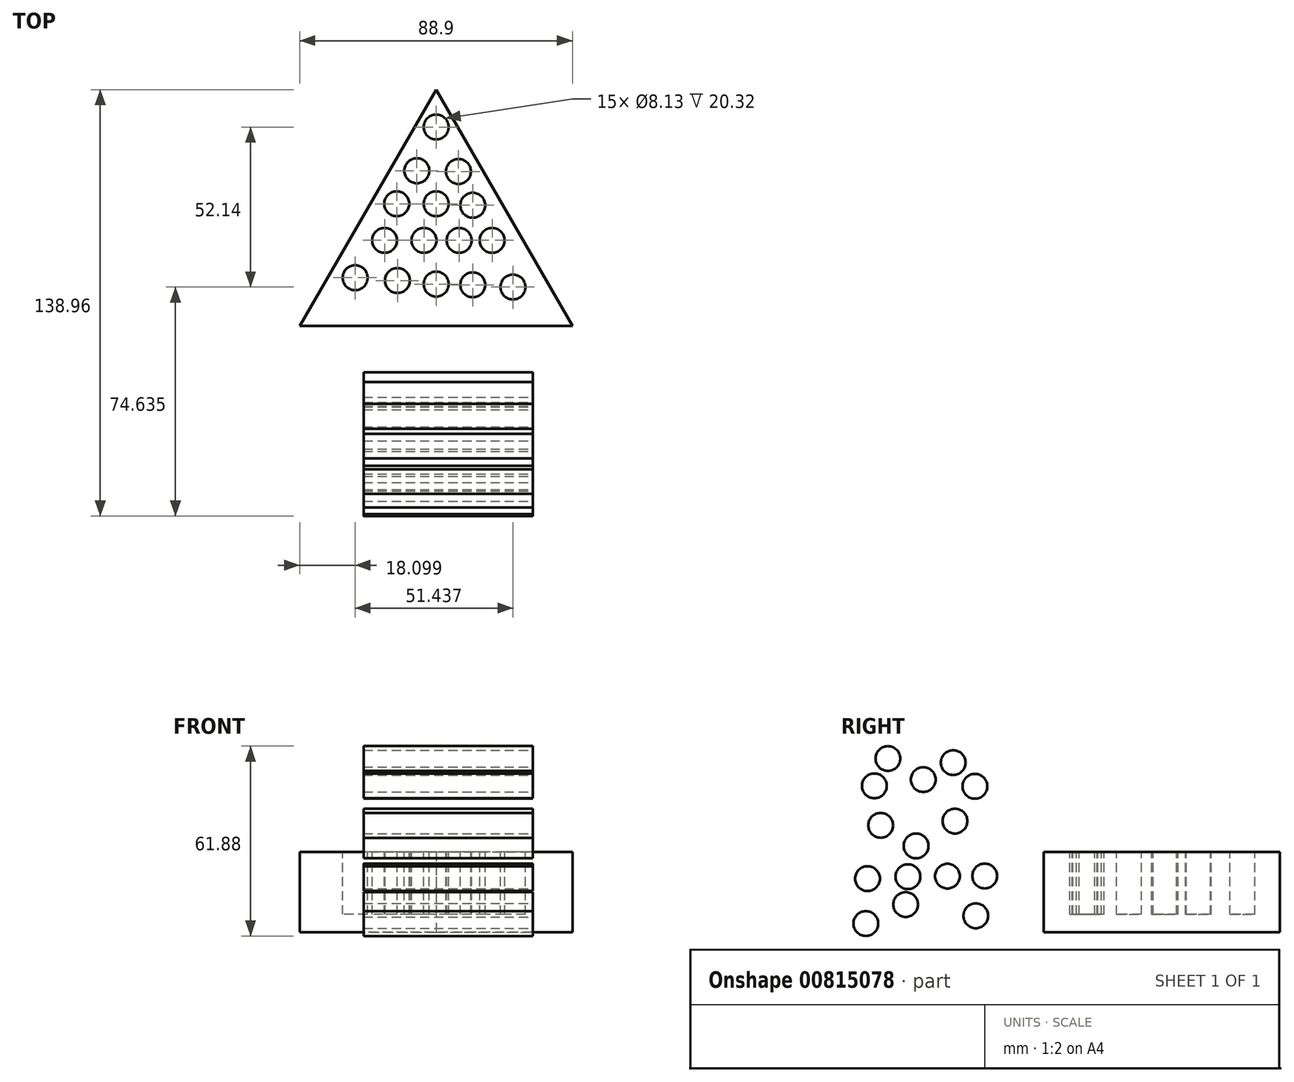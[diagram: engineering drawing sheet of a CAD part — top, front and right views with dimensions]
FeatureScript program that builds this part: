
annotation { "Feature Type Name" : "Feature", "Feature Type Description" : "" }
export const myFeature = defineFeature(function(context is Context, id is Id, definition is map)
    precondition{}
    {
        {
            var Q0;
            Q0=qCreatedBy(makeId("Top.planeOp"),FACE);
            var sketch = newSketch(context, id + "F0", { "sketchPlane" : qUnion([Q0])});
            skLineSegment(sketch, "E0", {"start": v(-75.96, 0) * mm, "end": v(-31.5, 76.99) * mm});
            skLineSegment(sketch, "E1", {"start": v(-31.5, 76.99) * mm, "end": v(12.94, 0) * mm});
            skLineSegment(sketch, "E2", {"start": v(12.94, 0) * mm, "end": v(-75.96, 0) * mm});
            skSolve(sketch);
        }
        {
            var Q0;
            Q0=qSketchRegion(id+"F0",true);
            var Q1;
            Q1=makeQuery(id+"F0.imprint","IMPRINT",FACE,{"disambiguationData":[TD([[makeQuery(id+"F0.imprint","IMPRINT",EDGE,{"derivedFrom":sQuery(id+"F0.wireOp",EDGE,"E0")}),-1.0]])]});
            extrude(context, id + "F1", {"entities" : qUnion([Q0, Q1]), "depth" : 26.16 * mm, "offsetDistance" : 25.4 * mm});
        }
        {
            var Q0;
            Q0=makeQuery(id+"F1.opExtrude","CAP_FACE",FACE,{"disambiguationData":[OSD([sQuery(id+"F0.wireOp",EDGE,"E0"),sQuery(id+"F0.wireOp",EDGE,"E1"),sQuery(id+"F0.wireOp",EDGE,"E2")])],"isStart":false});
            var sketch = newSketch(context, id + "F2", { "sketchPlane" : qUnion([Q0])});
            skCircle(sketch, "E3", {"center": v(-31.45, 64.8) * mm, "radius": 4.06 * mm});
            skCircle(sketch, "E4", {"center": v(-37.76, 50.54) * mm, "radius": 4.06 * mm});
            skCircle(sketch, "E5", {"center": v(-24.2, 50.3) * mm, "radius": 4.06 * mm});
            skCircle(sketch, "E6", {"center": v(-44.3, 39.79) * mm, "radius": 4.06 * mm});
            skCircle(sketch, "E7", {"center": v(-31.45, 39.79) * mm, "radius": 4.06 * mm});
            skCircle(sketch, "E8", {"center": v(-19.52, 39.32) * mm, "radius": 4.06 * mm});
            skCircle(sketch, "E9", {"center": v(-13.2, 27.87) * mm, "radius": 4.06 * mm});
            skCircle(sketch, "E10", {"center": v(-23.96, 27.87) * mm, "radius": 4.06 * mm});
            skCircle(sketch, "E11", {"center": v(-35.42, 27.87) * mm, "radius": 4.06 * mm});
            skCircle(sketch, "E12", {"center": v(-48.28, 27.87) * mm, "radius": 4.06 * mm});
            skCircle(sketch, "E13", {"center": v(-57.86, 15.7) * mm, "radius": 4.06 * mm});
            skCircle(sketch, "E14", {"center": v(-44.07, 14.77) * mm, "radius": 4.06 * mm});
            skCircle(sketch, "E15", {"center": v(-31.45, 13.6) * mm, "radius": 4.06 * mm});
            skCircle(sketch, "E16", {"center": v(-19.52, 13.37) * mm, "radius": 4.06 * mm});
            skCircle(sketch, "E17", {"center": v(-6.42, 12.66) * mm, "radius": 4.06 * mm});
            skSolve(sketch);
        }
        {
            var Q0;
            Q0=qSketchRegion(id+"F2",true);
            extrude(context, id + "F3", {"entities" : qUnion([Q0]), "operationType" : NewBodyOperationType.REMOVE, "oppositeDirection" : true, "depth" : 20.32 * mm, "offsetDistance" : 25.4 * mm});
        }
        {
            var Q0;
            Q0=qCreatedBy(makeId("Right.planeOp"),FACE);
            var sketch = newSketch(context, id + "F4", { "sketchPlane" : qUnion([Q0])});
            skCircle(sketch, "E18", {"center": v(-39.21, 49.8) * mm, "radius": 4.04 * mm});
            skCircle(sketch, "E19", {"center": v(-41.54, 28.18) * mm, "radius": 4.04 * mm});
            skCircle(sketch, "E20", {"center": v(-22.37, 47.6) * mm, "radius": 4.04 * mm});
            skCircle(sketch, "E21", {"center": v(-28.9, 36.26) * mm, "radius": 4.04 * mm});
            skCircle(sketch, "E22", {"center": v(-53.09, 34.88) * mm, "radius": 4.04 * mm});
            skCircle(sketch, "E23", {"center": v(-29.45, 55.32) * mm, "radius": 4.04 * mm});
            skCircle(sketch, "E24", {"center": v(-55.16, 47.76) * mm, "radius": 4.04 * mm});
            skCircle(sketch, "E25", {"center": v(-50.74, 56.67) * mm, "radius": 4.04 * mm});
            skCircle(sketch, "E26", {"center": v(-44.94, 9.07) * mm, "radius": 4.04 * mm});
            skCircle(sketch, "E27", {"center": v(-35.44, -4.98) * mm, "radius": 4.04 * mm});
            skCircle(sketch, "E28", {"center": v(-22.08, 5.4) * mm, "radius": 4.04 * mm});
            skCircle(sketch, "E29", {"center": v(-19.18, 18.36) * mm, "radius": 4.04 * mm});
            skCircle(sketch, "E30", {"center": v(-31.33, 18.32) * mm, "radius": 4.04 * mm});
            skCircle(sketch, "E31", {"center": v(-44.21, 18.14) * mm, "radius": 4.04 * mm});
            skCircle(sketch, "E32", {"center": v(-57.38, 17.52) * mm, "radius": 4.04 * mm});
            skCircle(sketch, "E33", {"center": v(-57.93, 2.87) * mm, "radius": 4.04 * mm});
            skCircle(sketch, "E34", {"center": v(-50.74, -11.04) * mm, "radius": 4.64 * mm});
            skSolve(sketch);
        }
        {
            var Q0;
            Q0=makeQuery(id+"F4.imprint","IMPRINT",FACE,{"disambiguationData":[TD([[makeQuery(id+"F4.imprint","IMPRINT",EDGE,{"derivedFrom":sQuery(id+"F4.wireOp",EDGE,"E18")}),1.0]])]});
            var Q1;
            Q1=makeQuery(id+"F4.imprint","IMPRINT",FACE,{"disambiguationData":[TD([[makeQuery(id+"F4.imprint","IMPRINT",EDGE,{"derivedFrom":sQuery(id+"F4.wireOp",EDGE,"E25")}),1.0]])]});
            var Q2;
            Q2=makeQuery(id+"F4.imprint","IMPRINT",FACE,{"disambiguationData":[TD([[makeQuery(id+"F4.imprint","IMPRINT",EDGE,{"derivedFrom":sQuery(id+"F4.wireOp",EDGE,"E24")}),1.0]])]});
            var Q3;
            Q3=makeQuery(id+"F4.imprint","IMPRINT",FACE,{"disambiguationData":[TD([[makeQuery(id+"F4.imprint","IMPRINT",EDGE,{"derivedFrom":sQuery(id+"F4.wireOp",EDGE,"E22")}),1.0]])]});
            var Q4;
            Q4=makeQuery(id+"F4.imprint","IMPRINT",FACE,{"disambiguationData":[TD([[makeQuery(id+"F4.imprint","IMPRINT",EDGE,{"derivedFrom":sQuery(id+"F4.wireOp",EDGE,"E20")}),1.0]])]});
            var Q5;
            Q5=makeQuery(id+"F4.imprint","IMPRINT",FACE,{"disambiguationData":[TD([[makeQuery(id+"F4.imprint","IMPRINT",EDGE,{"derivedFrom":sQuery(id+"F4.wireOp",EDGE,"E23")}),1.0]])]});
            var Q6;
            Q6=makeQuery(id+"F4.imprint","IMPRINT",FACE,{"disambiguationData":[TD([[makeQuery(id+"F4.imprint","IMPRINT",EDGE,{"derivedFrom":sQuery(id+"F4.wireOp",EDGE,"E21")}),1.0]])]});
            var Q7;
            Q7=makeQuery(id+"F4.imprint","IMPRINT",FACE,{"disambiguationData":[TD([[makeQuery(id+"F4.imprint","IMPRINT",EDGE,{"derivedFrom":sQuery(id+"F4.wireOp",EDGE,"E19")}),1.0]])]});
            var Q8;
            Q8=makeQuery(id+"F4.imprint","IMPRINT",FACE,{"disambiguationData":[TD([[makeQuery(id+"F4.imprint","IMPRINT",EDGE,{"derivedFrom":sQuery(id+"F4.wireOp",EDGE,"E31")}),1.0]])]});
            var Q9;
            Q9=makeQuery(id+"F4.imprint","IMPRINT",FACE,{"disambiguationData":[TD([[makeQuery(id+"F4.imprint","IMPRINT",EDGE,{"derivedFrom":sQuery(id+"F4.wireOp",EDGE,"E32")}),1.0]])]});
            var Q10;
            Q10=makeQuery(id+"F4.imprint","IMPRINT",FACE,{"disambiguationData":[TD([[makeQuery(id+"F4.imprint","IMPRINT",EDGE,{"derivedFrom":sQuery(id+"F4.wireOp",EDGE,"E26")}),1.0]])]});
            var Q11;
            Q11=makeQuery(id+"F4.imprint","IMPRINT",FACE,{"disambiguationData":[TD([[makeQuery(id+"F4.imprint","IMPRINT",EDGE,{"derivedFrom":sQuery(id+"F4.wireOp",EDGE,"E30")}),1.0]])]});
            var Q12;
            Q12=makeQuery(id+"F4.imprint","IMPRINT",FACE,{"disambiguationData":[TD([[makeQuery(id+"F4.imprint","IMPRINT",EDGE,{"derivedFrom":sQuery(id+"F4.wireOp",EDGE,"E29")}),1.0]])]});
            var Q13;
            Q13=makeQuery(id+"F4.imprint","IMPRINT",FACE,{"disambiguationData":[TD([[makeQuery(id+"F4.imprint","IMPRINT",EDGE,{"derivedFrom":sQuery(id+"F4.wireOp",EDGE,"E28")}),1.0]])]});
            var Q14;
            Q14=makeQuery(id+"F4.imprint","IMPRINT",FACE,{"disambiguationData":[TD([[makeQuery(id+"F4.imprint","IMPRINT",EDGE,{"derivedFrom":sQuery(id+"F4.wireOp",EDGE,"E33")}),1.0]])]});
            extrude(context, id + "F5", {"entities" : qUnion([Q0, Q1, Q2, Q3, Q4, Q5, Q6, Q7, Q8, Q9, Q10, Q11, Q12, Q13, Q14]), "oppositeDirection" : true, "depth" : 55.12 * mm, "offsetDistance" : 25.4 * mm});
        }
    });
